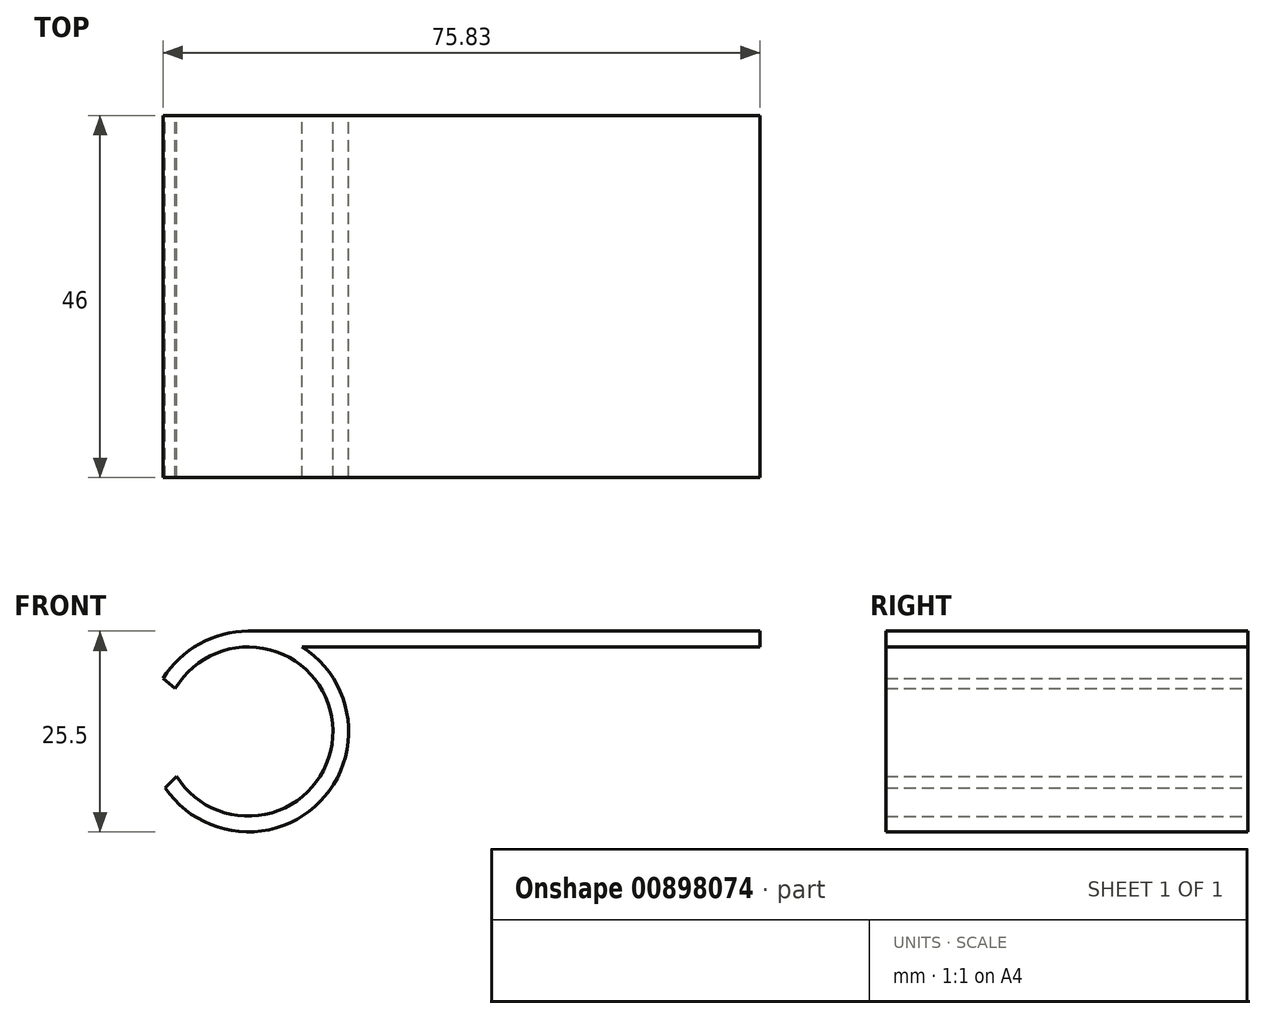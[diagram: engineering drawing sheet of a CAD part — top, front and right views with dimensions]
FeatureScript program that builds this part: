
annotation { "Feature Type Name" : "Feature", "Feature Type Description" : "" }
export const myFeature = defineFeature(function(context is Context, id is Id, definition is map)
    precondition{}
    {
        {
            var Q0;
            Q0=qCreatedBy(makeId("Front.planeOp"),FACE);
            var sketch = newSketch(context, id + "F0", { "sketchPlane" : qUnion([Q0])});
            skArc(sketch, "E0", {"start": v(-15.6, 32.1) * mm, "mid": v(4.28, 37.92) * mm, "end": v(-15.73, 43.23) * mm});
            skArc(sketch, "E1", {"start": v(-17.02, 30.64) * mm, "mid": v(2.67, 28.89) * mm, "end": v(0.39, 48.53) * mm});
            skLineSegment(sketch, "E2", {"start": v(0.39, 48.53) * mm, "end": v(58.53, 48.53) * mm});
            skLineSegment(sketch, "E3", {"start": v(58.53, 48.53) * mm, "end": v(58.53, 50.53) * mm});
            skLineSegment(sketch, "E4", {"start": v(58.53, 50.53) * mm, "end": v(-6.47, 50.53) * mm});
            skLineSegment(sketch, "E5", {"start": v(-15.6, 32.1) * mm, "end": v(-17.02, 30.64) * mm});
            skLineSegment(sketch, "E6", {"start": v(-15.73, 43.23) * mm, "end": v(-17.3, 44.5) * mm});
            skArc(sketch, "E7.trimOffspring", {"start": v(-6.47, 50.53) * mm, "mid": v(-12.66, 48.92) * mm, "end": v(-17.3, 44.5) * mm});
            skSolve(sketch);
        }
        {
            var Q0;
            Q0=makeQuery(id+"F0.imprint","IMPRINT",FACE,{"disambiguationData":[TD([[makeQuery(id+"F0.imprint","IMPRINT",EDGE,{"derivedFrom":sQuery(id+"F0.wireOp",EDGE,"E0")}),-1.0]])]});
            extrude(context, id + "F1", {"entities" : qUnion([Q0]), "depth" : 46 * mm, "offsetDistance" : 25 * mm});
        }
    });
